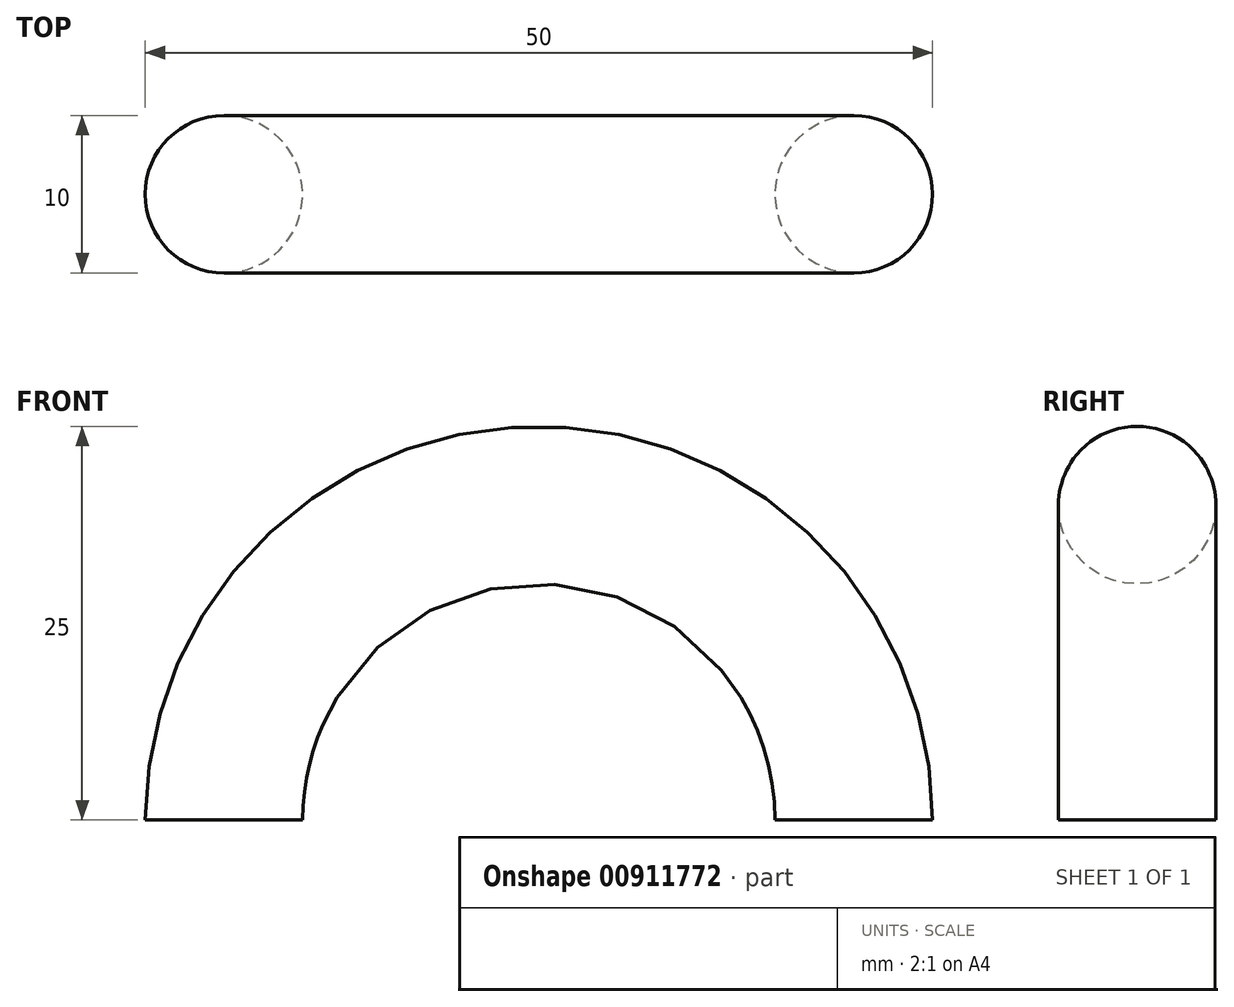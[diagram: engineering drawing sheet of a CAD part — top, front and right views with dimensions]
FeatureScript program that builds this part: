
annotation { "Feature Type Name" : "Feature", "Feature Type Description" : "" }
export const myFeature = defineFeature(function(context is Context, id is Id, definition is map)
    precondition{}
    {
        {
            var Q0;
            Q0=qCreatedBy(makeId("Top.planeOp"),FACE);
            var sketch = newSketch(context, id + "F0", { "sketchPlane" : qUnion([Q0])});
            skCircle(sketch, "E0", {"center": v(0, 0) * mm, "radius": 5 * mm});
            skLineSegment(sketch, "E1", {"start": v(-20, 14.2) * mm, "end": v(-20, -20.47) * mm});
            skSolve(sketch);
        }
        {
            var Q0;
            Q0=makeQuery(id+"F0.imprint","IMPRINT",FACE,{"disambiguationData":[TD([[makeQuery(id+"F0.imprint","IMPRINT",EDGE,{"derivedFrom":sQuery(id+"F0.wireOp",EDGE,"E0")}),1.0]])]});
            var Q1;
            Q1=sQuery(id+"F0.wireOp",EDGE,"E1");
            revolve(context, id + "F1", {"surfaceOperationType" : NewSurfaceOperationType.NEW, "entities" : qUnion([Q0]), "axis" : qUnion([Q1]), "revolveType" : RevolveType.ONE_DIRECTION, "angle" : 180 * degree});
        }
    });
